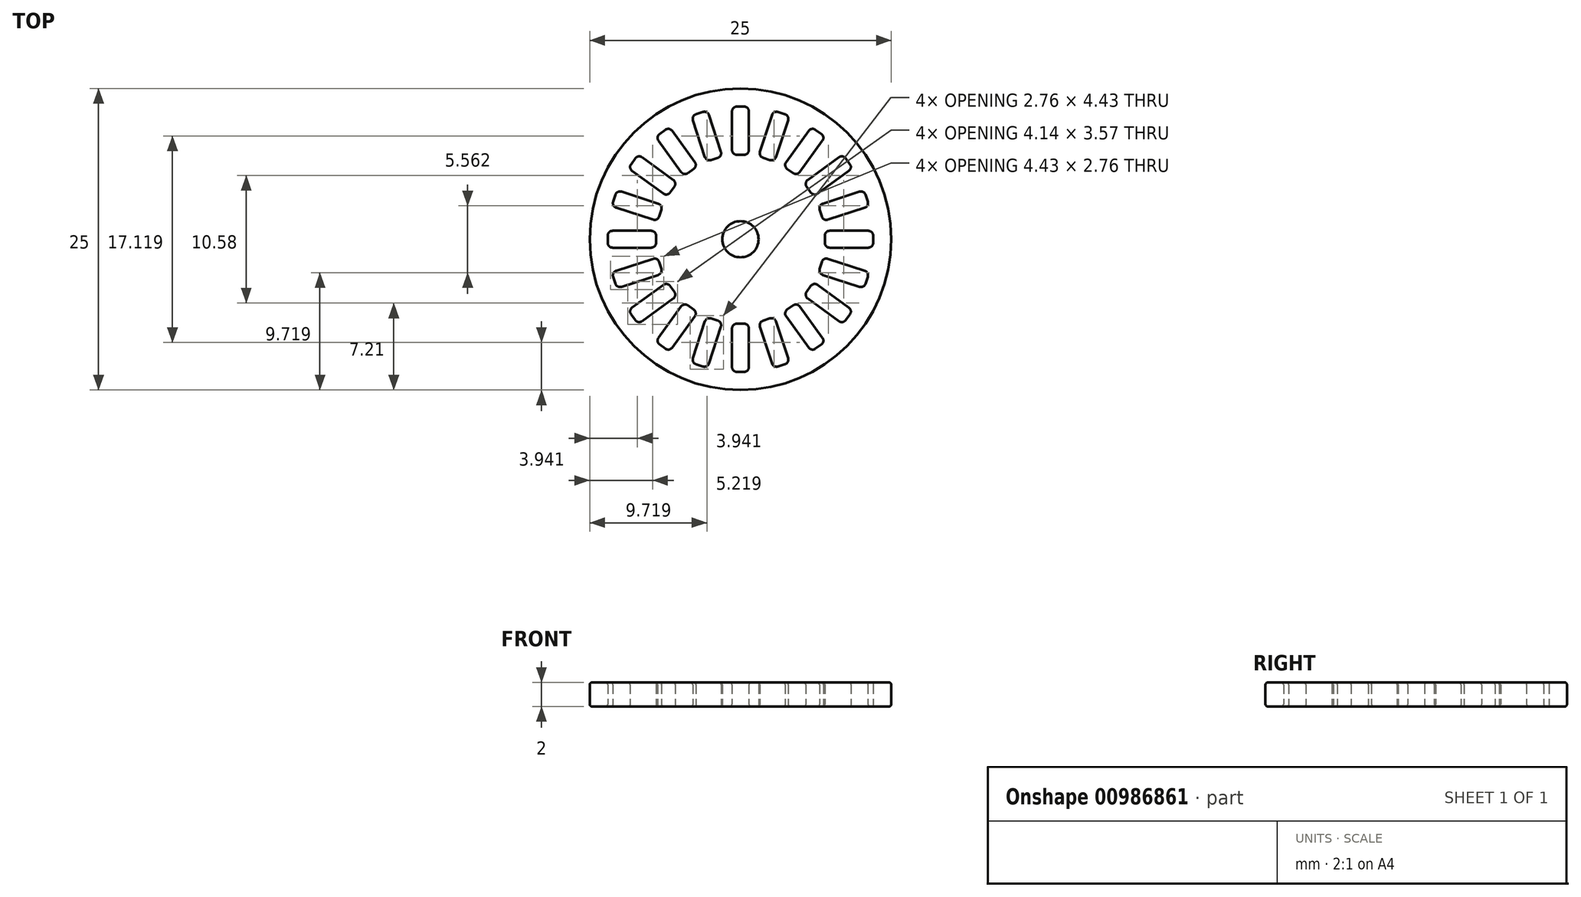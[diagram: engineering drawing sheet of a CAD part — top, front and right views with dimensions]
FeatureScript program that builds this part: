
annotation { "Feature Type Name" : "Feature", "Feature Type Description" : "" }
export const myFeature = defineFeature(function(context is Context, id is Id, definition is map)
    precondition{}
    {
        {
            var Q0;
            Q0=qCreatedBy(makeId("Top.planeOp"),FACE);
            var sketch = newSketch(context, id + "F0", { "sketchPlane" : qUnion([Q0])});
            skCircle(sketch, "E0", {"center": v(0, 0) * mm, "radius": 12.5 * mm});
            skCircle(sketch, "E1", {"center": v(0, 0) * mm, "radius": 9 * mm, "construction": true});
            skLineSegment(sketch, "E2.bottom", {"start": v(0.3, 11) * mm, "end": v(-0.3, 11) * mm});
            skLineSegment(sketch, "E2.top", {"start": v(0.3, 7) * mm, "end": v(-0.3, 7) * mm});
            skLineSegment(sketch, "E2.left", {"start": v(0.7, 10.6) * mm, "end": v(0.7, 7.4) * mm});
            skLineSegment(sketch, "E2.right", {"start": v(-0.7, 10.6) * mm, "end": v(-0.7, 7.4) * mm});
            skPoint(sketch, "E2.middle", {"position": v(0, 9) * mm});
            skPoint(sketch, "E3.visualSharp", {"position": v(-0.7, 11) * mm});
            skArc(sketch, "E3.filletArc", {"start": v(-0.3, 11) * mm, "mid": v(-0.58, 10.88) * mm, "end": v(-0.7, 10.6) * mm});
            skPoint(sketch, "E4.visualSharp", {"position": v(0.7, 11) * mm});
            skArc(sketch, "E4.filletArc", {"start": v(0.7, 10.6) * mm, "mid": v(0.58, 10.88) * mm, "end": v(0.3, 11) * mm});
            skPoint(sketch, "E5.visualSharp", {"position": v(0.7, 7) * mm});
            skArc(sketch, "E5.filletArc", {"start": v(0.3, 7) * mm, "mid": v(0.58, 7.12) * mm, "end": v(0.7, 7.4) * mm});
            skPoint(sketch, "E6.visualSharp", {"position": v(-0.7, 7) * mm});
            skArc(sketch, "E6.filletArc", {"start": v(-0.7, 7.4) * mm, "mid": v(-0.58, 7.12) * mm, "end": v(-0.3, 7) * mm});
            skLineSegment(sketch, "E7.1.0", {"start": v(-2.6, 10.3) * mm, "end": v(-1.62, 7.25) * mm});
            skPoint(sketch, "E7.1.1", {"position": v(-1.5, 6.87) * mm});
            skPoint(sketch, "E7.1.2", {"position": v(-2.78, 8.56) * mm});
            skPoint(sketch, "E7.1.3", {"position": v(-2.83, 6.44) * mm});
            skLineSegment(sketch, "E7.1.4", {"start": v(-3.94, 9.86) * mm, "end": v(-2.95, 6.82) * mm});
            skLineSegment(sketch, "E7.1.5", {"start": v(-1.88, 6.75) * mm, "end": v(-2.45, 6.56) * mm});
            skLineSegment(sketch, "E7.1.6", {"start": v(-3.11, 10.55) * mm, "end": v(-3.68, 10.37) * mm});
            skPoint(sketch, "E7.1.7", {"position": v(-4.06, 10.25) * mm});
            skPoint(sketch, "E7.1.8", {"position": v(-2.73, 10.68) * mm});
            skArc(sketch, "E7.1.9", {"start": v(-1.88, 6.75) * mm, "mid": v(-1.65, 6.95) * mm, "end": v(-1.62, 7.25) * mm});
            skArc(sketch, "E7.1.10", {"start": v(-3.68, 10.37) * mm, "mid": v(-3.92, 10.17) * mm, "end": v(-3.94, 9.86) * mm});
            skArc(sketch, "E7.1.11", {"start": v(-2.95, 6.82) * mm, "mid": v(-2.75, 6.59) * mm, "end": v(-2.45, 6.56) * mm});
            skArc(sketch, "E7.1.12", {"start": v(-2.6, 10.3) * mm, "mid": v(-2.8, 10.53) * mm, "end": v(-3.11, 10.55) * mm});
            skLineSegment(sketch, "E7.2.0", {"start": v(-5.66, 8.99) * mm, "end": v(-3.78, 6.4) * mm});
            skPoint(sketch, "E7.2.1", {"position": v(-3.55, 6.07) * mm});
            skPoint(sketch, "E7.2.2", {"position": v(-5.3, 7.28) * mm});
            skPoint(sketch, "E7.2.3", {"position": v(-4.68, 5.25) * mm});
            skLineSegment(sketch, "E7.2.4", {"start": v(-6.8, 8.16) * mm, "end": v(-4.92, 5.58) * mm});
            skLineSegment(sketch, "E7.2.5", {"start": v(-3.87, 5.84) * mm, "end": v(-4.36, 5.49) * mm});
            skLineSegment(sketch, "E7.2.6", {"start": v(-6.22, 9.08) * mm, "end": v(-6.7, 8.72) * mm});
            skPoint(sketch, "E7.2.7", {"position": v(-7.03, 8.49) * mm});
            skPoint(sketch, "E7.2.8", {"position": v(-5.9, 9.31) * mm});
            skArc(sketch, "E7.2.9", {"start": v(-3.87, 5.84) * mm, "mid": v(-3.71, 6.1) * mm, "end": v(-3.78, 6.4) * mm});
            skArc(sketch, "E7.2.10", {"start": v(-6.7, 8.72) * mm, "mid": v(-6.87, 8.46) * mm, "end": v(-6.8, 8.16) * mm});
            skArc(sketch, "E7.2.11", {"start": v(-4.92, 5.58) * mm, "mid": v(-4.65, 5.42) * mm, "end": v(-4.36, 5.49) * mm});
            skArc(sketch, "E7.2.12", {"start": v(-5.66, 8.99) * mm, "mid": v(-5.93, 9.15) * mm, "end": v(-6.22, 9.08) * mm});
            skLineSegment(sketch, "E7.3.0", {"start": v(-8.16, 6.8) * mm, "end": v(-5.58, 4.92) * mm});
            skPoint(sketch, "E7.3.1", {"position": v(-5.25, 4.68) * mm});
            skPoint(sketch, "E7.3.2", {"position": v(-7.28, 5.3) * mm});
            skPoint(sketch, "E7.3.3", {"position": v(-6.07, 3.55) * mm});
            skLineSegment(sketch, "E7.3.4", {"start": v(-8.99, 5.66) * mm, "end": v(-6.4, 3.78) * mm});
            skLineSegment(sketch, "E7.3.5", {"start": v(-5.49, 4.36) * mm, "end": v(-5.84, 3.87) * mm});
            skLineSegment(sketch, "E7.3.6", {"start": v(-8.72, 6.7) * mm, "end": v(-9.08, 6.22) * mm});
            skPoint(sketch, "E7.3.7", {"position": v(-9.31, 5.9) * mm});
            skPoint(sketch, "E7.3.8", {"position": v(-8.49, 7.03) * mm});
            skArc(sketch, "E7.3.9", {"start": v(-5.49, 4.36) * mm, "mid": v(-5.42, 4.65) * mm, "end": v(-5.58, 4.92) * mm});
            skArc(sketch, "E7.3.10", {"start": v(-9.08, 6.22) * mm, "mid": v(-9.15, 5.93) * mm, "end": v(-8.99, 5.66) * mm});
            skArc(sketch, "E7.3.11", {"start": v(-6.4, 3.78) * mm, "mid": v(-6.1, 3.71) * mm, "end": v(-5.84, 3.87) * mm});
            skArc(sketch, "E7.3.12", {"start": v(-8.16, 6.8) * mm, "mid": v(-8.46, 6.87) * mm, "end": v(-8.72, 6.7) * mm});
            skLineSegment(sketch, "E7.4.0", {"start": v(-9.86, 3.94) * mm, "end": v(-6.82, 2.95) * mm});
            skPoint(sketch, "E7.4.1", {"position": v(-6.44, 2.83) * mm});
            skPoint(sketch, "E7.4.2", {"position": v(-8.56, 2.78) * mm});
            skPoint(sketch, "E7.4.3", {"position": v(-6.87, 1.5) * mm});
            skLineSegment(sketch, "E7.4.4", {"start": v(-10.3, 2.6) * mm, "end": v(-7.25, 1.62) * mm});
            skLineSegment(sketch, "E7.4.5", {"start": v(-6.56, 2.45) * mm, "end": v(-6.75, 1.88) * mm});
            skLineSegment(sketch, "E7.4.6", {"start": v(-10.37, 3.68) * mm, "end": v(-10.55, 3.11) * mm});
            skPoint(sketch, "E7.4.7", {"position": v(-10.68, 2.73) * mm});
            skPoint(sketch, "E7.4.8", {"position": v(-10.25, 4.06) * mm});
            skArc(sketch, "E7.4.9", {"start": v(-6.56, 2.45) * mm, "mid": v(-6.59, 2.75) * mm, "end": v(-6.82, 2.95) * mm});
            skArc(sketch, "E7.4.10", {"start": v(-10.55, 3.11) * mm, "mid": v(-10.53, 2.8) * mm, "end": v(-10.3, 2.6) * mm});
            skArc(sketch, "E7.4.11", {"start": v(-7.25, 1.62) * mm, "mid": v(-6.95, 1.65) * mm, "end": v(-6.75, 1.88) * mm});
            skArc(sketch, "E7.4.12", {"start": v(-9.86, 3.94) * mm, "mid": v(-10.17, 3.92) * mm, "end": v(-10.37, 3.68) * mm});
            skLineSegment(sketch, "E7.5.0", {"start": v(-10.6, 0.7) * mm, "end": v(-7.4, 0.7) * mm});
            skPoint(sketch, "E7.5.1", {"position": v(-7, 0.7) * mm});
            skPoint(sketch, "E7.5.2", {"position": v(-9, 0) * mm});
            skPoint(sketch, "E7.5.3", {"position": v(-7, -0.7) * mm});
            skLineSegment(sketch, "E7.5.4", {"start": v(-10.6, -0.7) * mm, "end": v(-7.4, -0.7) * mm});
            skLineSegment(sketch, "E7.5.5", {"start": v(-7, 0.3) * mm, "end": v(-7, -0.3) * mm});
            skLineSegment(sketch, "E7.5.6", {"start": v(-11, 0.3) * mm, "end": v(-11, -0.3) * mm});
            skPoint(sketch, "E7.5.7", {"position": v(-11, -0.7) * mm});
            skPoint(sketch, "E7.5.8", {"position": v(-11, 0.7) * mm});
            skArc(sketch, "E7.5.9", {"start": v(-7, 0.3) * mm, "mid": v(-7.12, 0.58) * mm, "end": v(-7.4, 0.7) * mm});
            skArc(sketch, "E7.5.10", {"start": v(-11, -0.3) * mm, "mid": v(-10.88, -0.58) * mm, "end": v(-10.6, -0.7) * mm});
            skArc(sketch, "E7.5.11", {"start": v(-7.4, -0.7) * mm, "mid": v(-7.12, -0.58) * mm, "end": v(-7, -0.3) * mm});
            skArc(sketch, "E7.5.12", {"start": v(-10.6, 0.7) * mm, "mid": v(-10.88, 0.58) * mm, "end": v(-11, 0.3) * mm});
            skLineSegment(sketch, "E7.6.0", {"start": v(-10.3, -2.6) * mm, "end": v(-7.25, -1.62) * mm});
            skPoint(sketch, "E7.6.1", {"position": v(-6.87, -1.5) * mm});
            skPoint(sketch, "E7.6.2", {"position": v(-8.56, -2.78) * mm});
            skPoint(sketch, "E7.6.3", {"position": v(-6.44, -2.83) * mm});
            skLineSegment(sketch, "E7.6.4", {"start": v(-9.86, -3.94) * mm, "end": v(-6.82, -2.95) * mm});
            skLineSegment(sketch, "E7.6.5", {"start": v(-6.75, -1.88) * mm, "end": v(-6.56, -2.45) * mm});
            skLineSegment(sketch, "E7.6.6", {"start": v(-10.55, -3.11) * mm, "end": v(-10.37, -3.68) * mm});
            skPoint(sketch, "E7.6.7", {"position": v(-10.25, -4.06) * mm});
            skPoint(sketch, "E7.6.8", {"position": v(-10.68, -2.73) * mm});
            skArc(sketch, "E7.6.9", {"start": v(-6.75, -1.88) * mm, "mid": v(-6.95, -1.65) * mm, "end": v(-7.25, -1.62) * mm});
            skArc(sketch, "E7.6.10", {"start": v(-10.37, -3.68) * mm, "mid": v(-10.17, -3.92) * mm, "end": v(-9.86, -3.94) * mm});
            skArc(sketch, "E7.6.11", {"start": v(-6.82, -2.95) * mm, "mid": v(-6.59, -2.75) * mm, "end": v(-6.56, -2.45) * mm});
            skArc(sketch, "E7.6.12", {"start": v(-10.3, -2.6) * mm, "mid": v(-10.53, -2.8) * mm, "end": v(-10.55, -3.11) * mm});
            skLineSegment(sketch, "E7.7.0", {"start": v(-8.99, -5.66) * mm, "end": v(-6.4, -3.78) * mm});
            skPoint(sketch, "E7.7.1", {"position": v(-6.07, -3.55) * mm});
            skPoint(sketch, "E7.7.2", {"position": v(-7.28, -5.3) * mm});
            skPoint(sketch, "E7.7.3", {"position": v(-5.25, -4.68) * mm});
            skLineSegment(sketch, "E7.7.4", {"start": v(-8.16, -6.8) * mm, "end": v(-5.58, -4.92) * mm});
            skLineSegment(sketch, "E7.7.5", {"start": v(-5.84, -3.87) * mm, "end": v(-5.49, -4.36) * mm});
            skLineSegment(sketch, "E7.7.6", {"start": v(-9.08, -6.22) * mm, "end": v(-8.72, -6.7) * mm});
            skPoint(sketch, "E7.7.7", {"position": v(-8.49, -7.03) * mm});
            skPoint(sketch, "E7.7.8", {"position": v(-9.31, -5.9) * mm});
            skArc(sketch, "E7.7.9", {"start": v(-5.84, -3.87) * mm, "mid": v(-6.1, -3.71) * mm, "end": v(-6.4, -3.78) * mm});
            skArc(sketch, "E7.7.10", {"start": v(-8.72, -6.7) * mm, "mid": v(-8.46, -6.87) * mm, "end": v(-8.16, -6.8) * mm});
            skArc(sketch, "E7.7.11", {"start": v(-5.58, -4.92) * mm, "mid": v(-5.42, -4.65) * mm, "end": v(-5.49, -4.36) * mm});
            skArc(sketch, "E7.7.12", {"start": v(-8.99, -5.66) * mm, "mid": v(-9.15, -5.93) * mm, "end": v(-9.08, -6.22) * mm});
            skLineSegment(sketch, "E7.8.0", {"start": v(-6.8, -8.16) * mm, "end": v(-4.92, -5.58) * mm});
            skPoint(sketch, "E7.8.1", {"position": v(-4.68, -5.25) * mm});
            skPoint(sketch, "E7.8.2", {"position": v(-5.3, -7.28) * mm});
            skPoint(sketch, "E7.8.3", {"position": v(-3.55, -6.07) * mm});
            skLineSegment(sketch, "E7.8.4", {"start": v(-5.66, -8.99) * mm, "end": v(-3.78, -6.4) * mm});
            skLineSegment(sketch, "E7.8.5", {"start": v(-4.36, -5.49) * mm, "end": v(-3.87, -5.84) * mm});
            skLineSegment(sketch, "E7.8.6", {"start": v(-6.7, -8.72) * mm, "end": v(-6.22, -9.08) * mm});
            skPoint(sketch, "E7.8.7", {"position": v(-5.9, -9.31) * mm});
            skPoint(sketch, "E7.8.8", {"position": v(-7.03, -8.49) * mm});
            skArc(sketch, "E7.8.9", {"start": v(-4.36, -5.49) * mm, "mid": v(-4.65, -5.42) * mm, "end": v(-4.92, -5.58) * mm});
            skArc(sketch, "E7.8.10", {"start": v(-6.22, -9.08) * mm, "mid": v(-5.93, -9.15) * mm, "end": v(-5.66, -8.99) * mm});
            skArc(sketch, "E7.8.11", {"start": v(-3.78, -6.4) * mm, "mid": v(-3.71, -6.1) * mm, "end": v(-3.87, -5.84) * mm});
            skArc(sketch, "E7.8.12", {"start": v(-6.8, -8.16) * mm, "mid": v(-6.87, -8.46) * mm, "end": v(-6.7, -8.72) * mm});
            skLineSegment(sketch, "E7.9.0", {"start": v(-3.94, -9.86) * mm, "end": v(-2.95, -6.82) * mm});
            skPoint(sketch, "E7.9.1", {"position": v(-2.83, -6.44) * mm});
            skPoint(sketch, "E7.9.2", {"position": v(-2.78, -8.56) * mm});
            skPoint(sketch, "E7.9.3", {"position": v(-1.5, -6.87) * mm});
            skLineSegment(sketch, "E7.9.4", {"start": v(-2.6, -10.3) * mm, "end": v(-1.62, -7.25) * mm});
            skLineSegment(sketch, "E7.9.5", {"start": v(-2.45, -6.56) * mm, "end": v(-1.88, -6.75) * mm});
            skLineSegment(sketch, "E7.9.6", {"start": v(-3.68, -10.37) * mm, "end": v(-3.11, -10.55) * mm});
            skPoint(sketch, "E7.9.7", {"position": v(-2.73, -10.68) * mm});
            skPoint(sketch, "E7.9.8", {"position": v(-4.06, -10.25) * mm});
            skArc(sketch, "E7.9.9", {"start": v(-2.45, -6.56) * mm, "mid": v(-2.75, -6.59) * mm, "end": v(-2.95, -6.82) * mm});
            skArc(sketch, "E7.9.10", {"start": v(-3.11, -10.55) * mm, "mid": v(-2.8, -10.53) * mm, "end": v(-2.6, -10.3) * mm});
            skArc(sketch, "E7.9.11", {"start": v(-1.62, -7.25) * mm, "mid": v(-1.65, -6.95) * mm, "end": v(-1.88, -6.75) * mm});
            skArc(sketch, "E7.9.12", {"start": v(-3.94, -9.86) * mm, "mid": v(-3.92, -10.17) * mm, "end": v(-3.68, -10.37) * mm});
            skLineSegment(sketch, "E7.10.0", {"start": v(-0.7, -10.6) * mm, "end": v(-0.7, -7.4) * mm});
            skPoint(sketch, "E7.10.1", {"position": v(-0.7, -7) * mm});
            skPoint(sketch, "E7.10.2", {"position": v(0, -9) * mm});
            skPoint(sketch, "E7.10.3", {"position": v(0.7, -7) * mm});
            skLineSegment(sketch, "E7.10.4", {"start": v(0.7, -10.6) * mm, "end": v(0.7, -7.4) * mm});
            skLineSegment(sketch, "E7.10.5", {"start": v(-0.3, -7) * mm, "end": v(0.3, -7) * mm});
            skLineSegment(sketch, "E7.10.6", {"start": v(-0.3, -11) * mm, "end": v(0.3, -11) * mm});
            skPoint(sketch, "E7.10.7", {"position": v(0.7, -11) * mm});
            skPoint(sketch, "E7.10.8", {"position": v(-0.7, -11) * mm});
            skArc(sketch, "E7.10.9", {"start": v(-0.3, -7) * mm, "mid": v(-0.58, -7.12) * mm, "end": v(-0.7, -7.4) * mm});
            skArc(sketch, "E7.10.10", {"start": v(0.3, -11) * mm, "mid": v(0.58, -10.88) * mm, "end": v(0.7, -10.6) * mm});
            skArc(sketch, "E7.10.11", {"start": v(0.7, -7.4) * mm, "mid": v(0.58, -7.12) * mm, "end": v(0.3, -7) * mm});
            skArc(sketch, "E7.10.12", {"start": v(-0.7, -10.6) * mm, "mid": v(-0.58, -10.88) * mm, "end": v(-0.3, -11) * mm});
            skLineSegment(sketch, "E7.11.0", {"start": v(2.6, -10.3) * mm, "end": v(1.62, -7.25) * mm});
            skPoint(sketch, "E7.11.1", {"position": v(1.5, -6.87) * mm});
            skPoint(sketch, "E7.11.2", {"position": v(2.78, -8.56) * mm});
            skPoint(sketch, "E7.11.3", {"position": v(2.83, -6.44) * mm});
            skLineSegment(sketch, "E7.11.4", {"start": v(3.94, -9.86) * mm, "end": v(2.95, -6.82) * mm});
            skLineSegment(sketch, "E7.11.5", {"start": v(1.88, -6.75) * mm, "end": v(2.45, -6.56) * mm});
            skLineSegment(sketch, "E7.11.6", {"start": v(3.11, -10.55) * mm, "end": v(3.68, -10.37) * mm});
            skPoint(sketch, "E7.11.7", {"position": v(4.06, -10.25) * mm});
            skPoint(sketch, "E7.11.8", {"position": v(2.73, -10.68) * mm});
            skArc(sketch, "E7.11.9", {"start": v(1.88, -6.75) * mm, "mid": v(1.65, -6.95) * mm, "end": v(1.62, -7.25) * mm});
            skArc(sketch, "E7.11.10", {"start": v(3.68, -10.37) * mm, "mid": v(3.92, -10.17) * mm, "end": v(3.94, -9.86) * mm});
            skArc(sketch, "E7.11.11", {"start": v(2.95, -6.82) * mm, "mid": v(2.75, -6.59) * mm, "end": v(2.45, -6.56) * mm});
            skArc(sketch, "E7.11.12", {"start": v(2.6, -10.3) * mm, "mid": v(2.8, -10.53) * mm, "end": v(3.11, -10.55) * mm});
            skLineSegment(sketch, "E7.12.0", {"start": v(5.66, -8.99) * mm, "end": v(3.78, -6.4) * mm});
            skPoint(sketch, "E7.12.1", {"position": v(3.55, -6.07) * mm});
            skPoint(sketch, "E7.12.2", {"position": v(5.3, -7.28) * mm});
            skPoint(sketch, "E7.12.3", {"position": v(4.68, -5.25) * mm});
            skLineSegment(sketch, "E7.12.4", {"start": v(6.8, -8.16) * mm, "end": v(4.92, -5.58) * mm});
            skLineSegment(sketch, "E7.12.5", {"start": v(3.87, -5.84) * mm, "end": v(4.36, -5.49) * mm});
            skLineSegment(sketch, "E7.12.6", {"start": v(6.22, -9.08) * mm, "end": v(6.7, -8.72) * mm});
            skPoint(sketch, "E7.12.7", {"position": v(7.03, -8.49) * mm});
            skPoint(sketch, "E7.12.8", {"position": v(5.9, -9.31) * mm});
            skArc(sketch, "E7.12.9", {"start": v(3.87, -5.84) * mm, "mid": v(3.71, -6.1) * mm, "end": v(3.78, -6.4) * mm});
            skArc(sketch, "E7.12.10", {"start": v(6.7, -8.72) * mm, "mid": v(6.87, -8.46) * mm, "end": v(6.8, -8.16) * mm});
            skArc(sketch, "E7.12.11", {"start": v(4.92, -5.58) * mm, "mid": v(4.65, -5.42) * mm, "end": v(4.36, -5.49) * mm});
            skArc(sketch, "E7.12.12", {"start": v(5.66, -8.99) * mm, "mid": v(5.93, -9.15) * mm, "end": v(6.22, -9.08) * mm});
            skLineSegment(sketch, "E7.13.0", {"start": v(8.16, -6.8) * mm, "end": v(5.58, -4.92) * mm});
            skPoint(sketch, "E7.13.1", {"position": v(5.25, -4.68) * mm});
            skPoint(sketch, "E7.13.2", {"position": v(7.28, -5.3) * mm});
            skPoint(sketch, "E7.13.3", {"position": v(6.07, -3.55) * mm});
            skLineSegment(sketch, "E7.13.4", {"start": v(8.99, -5.66) * mm, "end": v(6.4, -3.78) * mm});
            skLineSegment(sketch, "E7.13.5", {"start": v(5.49, -4.36) * mm, "end": v(5.84, -3.87) * mm});
            skLineSegment(sketch, "E7.13.6", {"start": v(8.72, -6.7) * mm, "end": v(9.08, -6.22) * mm});
            skPoint(sketch, "E7.13.7", {"position": v(9.31, -5.9) * mm});
            skPoint(sketch, "E7.13.8", {"position": v(8.49, -7.03) * mm});
            skArc(sketch, "E7.13.9", {"start": v(5.49, -4.36) * mm, "mid": v(5.42, -4.65) * mm, "end": v(5.58, -4.92) * mm});
            skArc(sketch, "E7.13.10", {"start": v(9.08, -6.22) * mm, "mid": v(9.15, -5.93) * mm, "end": v(8.99, -5.66) * mm});
            skArc(sketch, "E7.13.11", {"start": v(6.4, -3.78) * mm, "mid": v(6.1, -3.71) * mm, "end": v(5.84, -3.87) * mm});
            skArc(sketch, "E7.13.12", {"start": v(8.16, -6.8) * mm, "mid": v(8.46, -6.87) * mm, "end": v(8.72, -6.7) * mm});
            skLineSegment(sketch, "E7.14.0", {"start": v(9.86, -3.94) * mm, "end": v(6.82, -2.95) * mm});
            skPoint(sketch, "E7.14.1", {"position": v(6.44, -2.83) * mm});
            skPoint(sketch, "E7.14.2", {"position": v(8.56, -2.78) * mm});
            skPoint(sketch, "E7.14.3", {"position": v(6.87, -1.5) * mm});
            skLineSegment(sketch, "E7.14.4", {"start": v(10.3, -2.6) * mm, "end": v(7.25, -1.62) * mm});
            skLineSegment(sketch, "E7.14.5", {"start": v(6.56, -2.45) * mm, "end": v(6.75, -1.88) * mm});
            skLineSegment(sketch, "E7.14.6", {"start": v(10.37, -3.68) * mm, "end": v(10.55, -3.11) * mm});
            skPoint(sketch, "E7.14.7", {"position": v(10.68, -2.73) * mm});
            skPoint(sketch, "E7.14.8", {"position": v(10.25, -4.06) * mm});
            skArc(sketch, "E7.14.9", {"start": v(6.56, -2.45) * mm, "mid": v(6.59, -2.75) * mm, "end": v(6.82, -2.95) * mm});
            skArc(sketch, "E7.14.10", {"start": v(10.55, -3.11) * mm, "mid": v(10.53, -2.8) * mm, "end": v(10.3, -2.6) * mm});
            skArc(sketch, "E7.14.11", {"start": v(7.25, -1.62) * mm, "mid": v(6.95, -1.65) * mm, "end": v(6.75, -1.88) * mm});
            skArc(sketch, "E7.14.12", {"start": v(9.86, -3.94) * mm, "mid": v(10.17, -3.92) * mm, "end": v(10.37, -3.68) * mm});
            skLineSegment(sketch, "E7.15.0", {"start": v(10.6, -0.7) * mm, "end": v(7.4, -0.7) * mm});
            skPoint(sketch, "E7.15.1", {"position": v(7, -0.7) * mm});
            skPoint(sketch, "E7.15.2", {"position": v(9, 0) * mm});
            skPoint(sketch, "E7.15.3", {"position": v(7, 0.7) * mm});
            skLineSegment(sketch, "E7.15.4", {"start": v(10.6, 0.7) * mm, "end": v(7.4, 0.7) * mm});
            skLineSegment(sketch, "E7.15.5", {"start": v(7, -0.3) * mm, "end": v(7, 0.3) * mm});
            skLineSegment(sketch, "E7.15.6", {"start": v(11, -0.3) * mm, "end": v(11, 0.3) * mm});
            skPoint(sketch, "E7.15.7", {"position": v(11, 0.7) * mm});
            skPoint(sketch, "E7.15.8", {"position": v(11, -0.7) * mm});
            skArc(sketch, "E7.15.9", {"start": v(7, -0.3) * mm, "mid": v(7.12, -0.58) * mm, "end": v(7.4, -0.7) * mm});
            skArc(sketch, "E7.15.10", {"start": v(11, 0.3) * mm, "mid": v(10.88, 0.58) * mm, "end": v(10.6, 0.7) * mm});
            skArc(sketch, "E7.15.11", {"start": v(7.4, 0.7) * mm, "mid": v(7.12, 0.58) * mm, "end": v(7, 0.3) * mm});
            skArc(sketch, "E7.15.12", {"start": v(10.6, -0.7) * mm, "mid": v(10.88, -0.58) * mm, "end": v(11, -0.3) * mm});
            skLineSegment(sketch, "E7.16.0", {"start": v(10.3, 2.6) * mm, "end": v(7.25, 1.62) * mm});
            skPoint(sketch, "E7.16.1", {"position": v(6.87, 1.5) * mm});
            skPoint(sketch, "E7.16.2", {"position": v(8.56, 2.78) * mm});
            skPoint(sketch, "E7.16.3", {"position": v(6.44, 2.83) * mm});
            skLineSegment(sketch, "E7.16.4", {"start": v(9.86, 3.94) * mm, "end": v(6.82, 2.95) * mm});
            skLineSegment(sketch, "E7.16.5", {"start": v(6.75, 1.88) * mm, "end": v(6.56, 2.45) * mm});
            skLineSegment(sketch, "E7.16.6", {"start": v(10.55, 3.11) * mm, "end": v(10.37, 3.68) * mm});
            skPoint(sketch, "E7.16.7", {"position": v(10.25, 4.06) * mm});
            skPoint(sketch, "E7.16.8", {"position": v(10.68, 2.73) * mm});
            skArc(sketch, "E7.16.9", {"start": v(6.75, 1.88) * mm, "mid": v(6.95, 1.65) * mm, "end": v(7.25, 1.62) * mm});
            skArc(sketch, "E7.16.10", {"start": v(10.37, 3.68) * mm, "mid": v(10.17, 3.92) * mm, "end": v(9.86, 3.94) * mm});
            skArc(sketch, "E7.16.11", {"start": v(6.82, 2.95) * mm, "mid": v(6.59, 2.75) * mm, "end": v(6.56, 2.45) * mm});
            skArc(sketch, "E7.16.12", {"start": v(10.3, 2.6) * mm, "mid": v(10.53, 2.8) * mm, "end": v(10.55, 3.11) * mm});
            skLineSegment(sketch, "E7.17.0", {"start": v(8.99, 5.66) * mm, "end": v(6.4, 3.78) * mm});
            skPoint(sketch, "E7.17.1", {"position": v(6.07, 3.55) * mm});
            skPoint(sketch, "E7.17.2", {"position": v(7.28, 5.3) * mm});
            skPoint(sketch, "E7.17.3", {"position": v(5.25, 4.68) * mm});
            skLineSegment(sketch, "E7.17.4", {"start": v(8.16, 6.8) * mm, "end": v(5.58, 4.92) * mm});
            skLineSegment(sketch, "E7.17.5", {"start": v(5.84, 3.87) * mm, "end": v(5.49, 4.36) * mm});
            skLineSegment(sketch, "E7.17.6", {"start": v(9.08, 6.22) * mm, "end": v(8.72, 6.7) * mm});
            skPoint(sketch, "E7.17.7", {"position": v(8.49, 7.03) * mm});
            skPoint(sketch, "E7.17.8", {"position": v(9.31, 5.9) * mm});
            skArc(sketch, "E7.17.9", {"start": v(5.84, 3.87) * mm, "mid": v(6.1, 3.71) * mm, "end": v(6.4, 3.78) * mm});
            skArc(sketch, "E7.17.10", {"start": v(8.72, 6.7) * mm, "mid": v(8.46, 6.87) * mm, "end": v(8.16, 6.8) * mm});
            skArc(sketch, "E7.17.11", {"start": v(5.58, 4.92) * mm, "mid": v(5.42, 4.65) * mm, "end": v(5.49, 4.36) * mm});
            skArc(sketch, "E7.17.12", {"start": v(8.99, 5.66) * mm, "mid": v(9.15, 5.93) * mm, "end": v(9.08, 6.22) * mm});
            skLineSegment(sketch, "E7.18.0", {"start": v(6.8, 8.16) * mm, "end": v(4.92, 5.58) * mm});
            skPoint(sketch, "E7.18.1", {"position": v(4.68, 5.25) * mm});
            skPoint(sketch, "E7.18.2", {"position": v(5.3, 7.28) * mm});
            skPoint(sketch, "E7.18.3", {"position": v(3.55, 6.07) * mm});
            skLineSegment(sketch, "E7.18.4", {"start": v(5.66, 8.99) * mm, "end": v(3.78, 6.4) * mm});
            skLineSegment(sketch, "E7.18.5", {"start": v(4.36, 5.49) * mm, "end": v(3.87, 5.84) * mm});
            skLineSegment(sketch, "E7.18.6", {"start": v(6.7, 8.72) * mm, "end": v(6.22, 9.08) * mm});
            skPoint(sketch, "E7.18.7", {"position": v(5.9, 9.31) * mm});
            skPoint(sketch, "E7.18.8", {"position": v(7.03, 8.49) * mm});
            skArc(sketch, "E7.18.9", {"start": v(4.36, 5.49) * mm, "mid": v(4.65, 5.42) * mm, "end": v(4.92, 5.58) * mm});
            skArc(sketch, "E7.18.10", {"start": v(6.22, 9.08) * mm, "mid": v(5.93, 9.15) * mm, "end": v(5.66, 8.99) * mm});
            skArc(sketch, "E7.18.11", {"start": v(3.78, 6.4) * mm, "mid": v(3.71, 6.1) * mm, "end": v(3.87, 5.84) * mm});
            skArc(sketch, "E7.18.12", {"start": v(6.8, 8.16) * mm, "mid": v(6.87, 8.46) * mm, "end": v(6.7, 8.72) * mm});
            skLineSegment(sketch, "E7.19.0", {"start": v(3.94, 9.86) * mm, "end": v(2.95, 6.82) * mm});
            skPoint(sketch, "E7.19.1", {"position": v(2.83, 6.44) * mm});
            skPoint(sketch, "E7.19.2", {"position": v(2.78, 8.56) * mm});
            skPoint(sketch, "E7.19.3", {"position": v(1.5, 6.87) * mm});
            skLineSegment(sketch, "E7.19.4", {"start": v(2.6, 10.3) * mm, "end": v(1.62, 7.25) * mm});
            skLineSegment(sketch, "E7.19.5", {"start": v(2.45, 6.56) * mm, "end": v(1.88, 6.75) * mm});
            skLineSegment(sketch, "E7.19.6", {"start": v(3.68, 10.37) * mm, "end": v(3.11, 10.55) * mm});
            skPoint(sketch, "E7.19.7", {"position": v(2.73, 10.68) * mm});
            skPoint(sketch, "E7.19.8", {"position": v(4.06, 10.25) * mm});
            skArc(sketch, "E7.19.9", {"start": v(2.45, 6.56) * mm, "mid": v(2.75, 6.59) * mm, "end": v(2.95, 6.82) * mm});
            skArc(sketch, "E7.19.10", {"start": v(3.11, 10.55) * mm, "mid": v(2.8, 10.53) * mm, "end": v(2.6, 10.3) * mm});
            skArc(sketch, "E7.19.11", {"start": v(1.62, 7.25) * mm, "mid": v(1.65, 6.95) * mm, "end": v(1.88, 6.75) * mm});
            skArc(sketch, "E7.19.12", {"start": v(3.94, 9.86) * mm, "mid": v(3.92, 10.17) * mm, "end": v(3.68, 10.37) * mm});
            skCircle(sketch, "E8", {"center": v(0, 0) * mm, "radius": 1.5 * mm});
            skSolve(sketch);
        }
        {
            var Q0;
            Q0=makeQuery(id+"F0.imprint","IMPRINT",FACE,{"disambiguationData":[TD([[makeQuery(id+"F0.imprint","IMPRINT",EDGE,{"derivedFrom":sQuery(id+"F0.wireOp",EDGE,"E0")}),1.0]])]});
            extrude(context, id + "F1", {"entities" : qUnion([Q0]), "depth" : 2 * mm, "offsetDistance" : 25 * mm});
        }
        {
            var Q0;
            Q0=makeQuery(id+"F1.opExtrude","CAP_FACE",FACE,{"disambiguationData":[OSD([sQuery(id+"F0.wireOp",EDGE,"E0"),sQuery(id+"F0.wireOp",EDGE,"E2.bottom"),sQuery(id+"F0.wireOp",EDGE,"E2.top"),sQuery(id+"F0.wireOp",EDGE,"E2.left"),sQuery(id+"F0.wireOp",EDGE,"E2.right"),sQuery(id+"F0.wireOp",EDGE,"E3.filletArc"),sQuery(id+"F0.wireOp",EDGE,"E4.filletArc"),sQuery(id+"F0.wireOp",EDGE,"E5.filletArc"),sQuery(id+"F0.wireOp",EDGE,"E6.filletArc"),sQuery(id+"F0.wireOp",EDGE,"E7.1.0"),sQuery(id+"F0.wireOp",EDGE,"E7.1.4"),sQuery(id+"F0.wireOp",EDGE,"E7.1.5"),sQuery(id+"F0.wireOp",EDGE,"E7.1.6"),sQuery(id+"F0.wireOp",EDGE,"E7.1.9"),sQuery(id+"F0.wireOp",EDGE,"E7.1.10"),sQuery(id+"F0.wireOp",EDGE,"E7.1.11"),sQuery(id+"F0.wireOp",EDGE,"E7.1.12"),sQuery(id+"F0.wireOp",EDGE,"E7.2.0"),sQuery(id+"F0.wireOp",EDGE,"E7.2.4"),sQuery(id+"F0.wireOp",EDGE,"E7.2.5"),sQuery(id+"F0.wireOp",EDGE,"E7.2.6"),sQuery(id+"F0.wireOp",EDGE,"E7.2.9"),sQuery(id+"F0.wireOp",EDGE,"E7.2.10"),sQuery(id+"F0.wireOp",EDGE,"E7.2.11"),sQuery(id+"F0.wireOp",EDGE,"E7.2.12"),sQuery(id+"F0.wireOp",EDGE,"E7.3.0"),sQuery(id+"F0.wireOp",EDGE,"E7.3.4"),sQuery(id+"F0.wireOp",EDGE,"E7.3.5"),sQuery(id+"F0.wireOp",EDGE,"E7.3.6"),sQuery(id+"F0.wireOp",EDGE,"E7.3.9"),sQuery(id+"F0.wireOp",EDGE,"E7.3.10"),sQuery(id+"F0.wireOp",EDGE,"E7.3.11"),sQuery(id+"F0.wireOp",EDGE,"E7.3.12"),sQuery(id+"F0.wireOp",EDGE,"E7.4.0"),sQuery(id+"F0.wireOp",EDGE,"E7.4.4"),sQuery(id+"F0.wireOp",EDGE,"E7.4.5"),sQuery(id+"F0.wireOp",EDGE,"E7.4.6"),sQuery(id+"F0.wireOp",EDGE,"E7.4.9"),sQuery(id+"F0.wireOp",EDGE,"E7.4.10"),sQuery(id+"F0.wireOp",EDGE,"E7.4.11"),sQuery(id+"F0.wireOp",EDGE,"E7.4.12"),sQuery(id+"F0.wireOp",EDGE,"E7.5.0"),sQuery(id+"F0.wireOp",EDGE,"E7.5.4"),sQuery(id+"F0.wireOp",EDGE,"E7.5.5"),sQuery(id+"F0.wireOp",EDGE,"E7.5.6"),sQuery(id+"F0.wireOp",EDGE,"E7.5.9"),sQuery(id+"F0.wireOp",EDGE,"E7.5.10"),sQuery(id+"F0.wireOp",EDGE,"E7.5.11"),sQuery(id+"F0.wireOp",EDGE,"E7.5.12"),sQuery(id+"F0.wireOp",EDGE,"E7.6.0"),sQuery(id+"F0.wireOp",EDGE,"E7.6.4"),sQuery(id+"F0.wireOp",EDGE,"E7.6.5"),sQuery(id+"F0.wireOp",EDGE,"E7.6.6"),sQuery(id+"F0.wireOp",EDGE,"E7.6.9"),sQuery(id+"F0.wireOp",EDGE,"E7.6.10"),sQuery(id+"F0.wireOp",EDGE,"E7.6.11"),sQuery(id+"F0.wireOp",EDGE,"E7.6.12"),sQuery(id+"F0.wireOp",EDGE,"E7.7.0"),sQuery(id+"F0.wireOp",EDGE,"E7.7.4"),sQuery(id+"F0.wireOp",EDGE,"E7.7.5"),sQuery(id+"F0.wireOp",EDGE,"E7.7.6"),sQuery(id+"F0.wireOp",EDGE,"E7.7.9"),sQuery(id+"F0.wireOp",EDGE,"E7.7.10"),sQuery(id+"F0.wireOp",EDGE,"E7.7.11"),sQuery(id+"F0.wireOp",EDGE,"E7.7.12"),sQuery(id+"F0.wireOp",EDGE,"E7.8.0"),sQuery(id+"F0.wireOp",EDGE,"E7.8.4"),sQuery(id+"F0.wireOp",EDGE,"E7.8.5"),sQuery(id+"F0.wireOp",EDGE,"E7.8.6"),sQuery(id+"F0.wireOp",EDGE,"E7.8.9"),sQuery(id+"F0.wireOp",EDGE,"E7.8.10"),sQuery(id+"F0.wireOp",EDGE,"E7.8.11"),sQuery(id+"F0.wireOp",EDGE,"E7.8.12"),sQuery(id+"F0.wireOp",EDGE,"E7.9.0"),sQuery(id+"F0.wireOp",EDGE,"E7.9.4"),sQuery(id+"F0.wireOp",EDGE,"E7.9.5"),sQuery(id+"F0.wireOp",EDGE,"E7.9.6"),sQuery(id+"F0.wireOp",EDGE,"E7.9.9"),sQuery(id+"F0.wireOp",EDGE,"E7.9.10"),sQuery(id+"F0.wireOp",EDGE,"E7.9.11"),sQuery(id+"F0.wireOp",EDGE,"E7.9.12"),sQuery(id+"F0.wireOp",EDGE,"E7.10.0"),sQuery(id+"F0.wireOp",EDGE,"E7.10.4"),sQuery(id+"F0.wireOp",EDGE,"E7.10.5"),sQuery(id+"F0.wireOp",EDGE,"E7.10.6"),sQuery(id+"F0.wireOp",EDGE,"E7.10.9"),sQuery(id+"F0.wireOp",EDGE,"E7.10.10"),sQuery(id+"F0.wireOp",EDGE,"E7.10.11"),sQuery(id+"F0.wireOp",EDGE,"E7.10.12"),sQuery(id+"F0.wireOp",EDGE,"E7.11.0"),sQuery(id+"F0.wireOp",EDGE,"E7.11.4"),sQuery(id+"F0.wireOp",EDGE,"E7.11.5"),sQuery(id+"F0.wireOp",EDGE,"E7.11.6"),sQuery(id+"F0.wireOp",EDGE,"E7.11.9"),sQuery(id+"F0.wireOp",EDGE,"E7.11.10"),sQuery(id+"F0.wireOp",EDGE,"E7.11.11"),sQuery(id+"F0.wireOp",EDGE,"E7.11.12"),sQuery(id+"F0.wireOp",EDGE,"E7.12.0"),sQuery(id+"F0.wireOp",EDGE,"E7.12.4"),sQuery(id+"F0.wireOp",EDGE,"E7.12.5"),sQuery(id+"F0.wireOp",EDGE,"E7.12.6"),sQuery(id+"F0.wireOp",EDGE,"E7.12.9"),sQuery(id+"F0.wireOp",EDGE,"E7.12.10"),sQuery(id+"F0.wireOp",EDGE,"E7.12.11"),sQuery(id+"F0.wireOp",EDGE,"E7.12.12"),sQuery(id+"F0.wireOp",EDGE,"E7.13.0"),sQuery(id+"F0.wireOp",EDGE,"E7.13.4"),sQuery(id+"F0.wireOp",EDGE,"E7.13.5"),sQuery(id+"F0.wireOp",EDGE,"E7.13.6"),sQuery(id+"F0.wireOp",EDGE,"E7.13.9"),sQuery(id+"F0.wireOp",EDGE,"E7.13.10"),sQuery(id+"F0.wireOp",EDGE,"E7.13.11"),sQuery(id+"F0.wireOp",EDGE,"E7.13.12"),sQuery(id+"F0.wireOp",EDGE,"E7.14.0"),sQuery(id+"F0.wireOp",EDGE,"E7.14.4"),sQuery(id+"F0.wireOp",EDGE,"E7.14.5"),sQuery(id+"F0.wireOp",EDGE,"E7.14.6"),sQuery(id+"F0.wireOp",EDGE,"E7.14.9"),sQuery(id+"F0.wireOp",EDGE,"E7.14.10"),sQuery(id+"F0.wireOp",EDGE,"E7.14.11"),sQuery(id+"F0.wireOp",EDGE,"E7.14.12"),sQuery(id+"F0.wireOp",EDGE,"E7.15.0"),sQuery(id+"F0.wireOp",EDGE,"E7.15.4"),sQuery(id+"F0.wireOp",EDGE,"E7.15.5"),sQuery(id+"F0.wireOp",EDGE,"E7.15.6"),sQuery(id+"F0.wireOp",EDGE,"E7.15.9"),sQuery(id+"F0.wireOp",EDGE,"E7.15.10"),sQuery(id+"F0.wireOp",EDGE,"E7.15.11"),sQuery(id+"F0.wireOp",EDGE,"E7.15.12"),sQuery(id+"F0.wireOp",EDGE,"E7.16.0"),sQuery(id+"F0.wireOp",EDGE,"E7.16.4"),sQuery(id+"F0.wireOp",EDGE,"E7.16.5"),sQuery(id+"F0.wireOp",EDGE,"E7.16.6"),sQuery(id+"F0.wireOp",EDGE,"E7.16.9"),sQuery(id+"F0.wireOp",EDGE,"E7.16.10"),sQuery(id+"F0.wireOp",EDGE,"E7.16.11"),sQuery(id+"F0.wireOp",EDGE,"E7.16.12"),sQuery(id+"F0.wireOp",EDGE,"E7.17.0"),sQuery(id+"F0.wireOp",EDGE,"E7.17.4"),sQuery(id+"F0.wireOp",EDGE,"E7.17.5"),sQuery(id+"F0.wireOp",EDGE,"E7.17.6"),sQuery(id+"F0.wireOp",EDGE,"E7.17.9"),sQuery(id+"F0.wireOp",EDGE,"E7.17.10"),sQuery(id+"F0.wireOp",EDGE,"E7.17.11"),sQuery(id+"F0.wireOp",EDGE,"E7.17.12"),sQuery(id+"F0.wireOp",EDGE,"E7.18.0"),sQuery(id+"F0.wireOp",EDGE,"E7.18.4"),sQuery(id+"F0.wireOp",EDGE,"E7.18.5"),sQuery(id+"F0.wireOp",EDGE,"E7.18.6"),sQuery(id+"F0.wireOp",EDGE,"E7.18.9"),sQuery(id+"F0.wireOp",EDGE,"E7.18.10"),sQuery(id+"F0.wireOp",EDGE,"E7.18.11"),sQuery(id+"F0.wireOp",EDGE,"E7.18.12"),sQuery(id+"F0.wireOp",EDGE,"E7.19.0"),sQuery(id+"F0.wireOp",EDGE,"E7.19.4"),sQuery(id+"F0.wireOp",EDGE,"E7.19.5"),sQuery(id+"F0.wireOp",EDGE,"E7.19.6"),sQuery(id+"F0.wireOp",EDGE,"E7.19.9"),sQuery(id+"F0.wireOp",EDGE,"E7.19.10"),sQuery(id+"F0.wireOp",EDGE,"E7.19.11"),sQuery(id+"F0.wireOp",EDGE,"E7.19.12")])],"isStart":false});
            var Q1;
            Q1=makeQuery(id+"F1.opExtrude","CAP_FACE",FACE,{"disambiguationData":[OSD([sQuery(id+"F0.wireOp",EDGE,"E0"),sQuery(id+"F0.wireOp",EDGE,"E2.bottom"),sQuery(id+"F0.wireOp",EDGE,"E2.top"),sQuery(id+"F0.wireOp",EDGE,"E2.left"),sQuery(id+"F0.wireOp",EDGE,"E2.right"),sQuery(id+"F0.wireOp",EDGE,"E3.filletArc"),sQuery(id+"F0.wireOp",EDGE,"E4.filletArc"),sQuery(id+"F0.wireOp",EDGE,"E5.filletArc"),sQuery(id+"F0.wireOp",EDGE,"E6.filletArc"),sQuery(id+"F0.wireOp",EDGE,"E7.1.0"),sQuery(id+"F0.wireOp",EDGE,"E7.1.4"),sQuery(id+"F0.wireOp",EDGE,"E7.1.5"),sQuery(id+"F0.wireOp",EDGE,"E7.1.6"),sQuery(id+"F0.wireOp",EDGE,"E7.1.9"),sQuery(id+"F0.wireOp",EDGE,"E7.1.10"),sQuery(id+"F0.wireOp",EDGE,"E7.1.11"),sQuery(id+"F0.wireOp",EDGE,"E7.1.12"),sQuery(id+"F0.wireOp",EDGE,"E7.2.0"),sQuery(id+"F0.wireOp",EDGE,"E7.2.4"),sQuery(id+"F0.wireOp",EDGE,"E7.2.5"),sQuery(id+"F0.wireOp",EDGE,"E7.2.6"),sQuery(id+"F0.wireOp",EDGE,"E7.2.9"),sQuery(id+"F0.wireOp",EDGE,"E7.2.10"),sQuery(id+"F0.wireOp",EDGE,"E7.2.11"),sQuery(id+"F0.wireOp",EDGE,"E7.2.12"),sQuery(id+"F0.wireOp",EDGE,"E7.3.0"),sQuery(id+"F0.wireOp",EDGE,"E7.3.4"),sQuery(id+"F0.wireOp",EDGE,"E7.3.5"),sQuery(id+"F0.wireOp",EDGE,"E7.3.6"),sQuery(id+"F0.wireOp",EDGE,"E7.3.9"),sQuery(id+"F0.wireOp",EDGE,"E7.3.10"),sQuery(id+"F0.wireOp",EDGE,"E7.3.11"),sQuery(id+"F0.wireOp",EDGE,"E7.3.12"),sQuery(id+"F0.wireOp",EDGE,"E7.4.0"),sQuery(id+"F0.wireOp",EDGE,"E7.4.4"),sQuery(id+"F0.wireOp",EDGE,"E7.4.5"),sQuery(id+"F0.wireOp",EDGE,"E7.4.6"),sQuery(id+"F0.wireOp",EDGE,"E7.4.9"),sQuery(id+"F0.wireOp",EDGE,"E7.4.10"),sQuery(id+"F0.wireOp",EDGE,"E7.4.11"),sQuery(id+"F0.wireOp",EDGE,"E7.4.12"),sQuery(id+"F0.wireOp",EDGE,"E7.5.0"),sQuery(id+"F0.wireOp",EDGE,"E7.5.4"),sQuery(id+"F0.wireOp",EDGE,"E7.5.5"),sQuery(id+"F0.wireOp",EDGE,"E7.5.6"),sQuery(id+"F0.wireOp",EDGE,"E7.5.9"),sQuery(id+"F0.wireOp",EDGE,"E7.5.10"),sQuery(id+"F0.wireOp",EDGE,"E7.5.11"),sQuery(id+"F0.wireOp",EDGE,"E7.5.12"),sQuery(id+"F0.wireOp",EDGE,"E7.6.0"),sQuery(id+"F0.wireOp",EDGE,"E7.6.4"),sQuery(id+"F0.wireOp",EDGE,"E7.6.5"),sQuery(id+"F0.wireOp",EDGE,"E7.6.6"),sQuery(id+"F0.wireOp",EDGE,"E7.6.9"),sQuery(id+"F0.wireOp",EDGE,"E7.6.10"),sQuery(id+"F0.wireOp",EDGE,"E7.6.11"),sQuery(id+"F0.wireOp",EDGE,"E7.6.12"),sQuery(id+"F0.wireOp",EDGE,"E7.7.0"),sQuery(id+"F0.wireOp",EDGE,"E7.7.4"),sQuery(id+"F0.wireOp",EDGE,"E7.7.5"),sQuery(id+"F0.wireOp",EDGE,"E7.7.6"),sQuery(id+"F0.wireOp",EDGE,"E7.7.9"),sQuery(id+"F0.wireOp",EDGE,"E7.7.10"),sQuery(id+"F0.wireOp",EDGE,"E7.7.11"),sQuery(id+"F0.wireOp",EDGE,"E7.7.12"),sQuery(id+"F0.wireOp",EDGE,"E7.8.0"),sQuery(id+"F0.wireOp",EDGE,"E7.8.4"),sQuery(id+"F0.wireOp",EDGE,"E7.8.5"),sQuery(id+"F0.wireOp",EDGE,"E7.8.6"),sQuery(id+"F0.wireOp",EDGE,"E7.8.9"),sQuery(id+"F0.wireOp",EDGE,"E7.8.10"),sQuery(id+"F0.wireOp",EDGE,"E7.8.11"),sQuery(id+"F0.wireOp",EDGE,"E7.8.12"),sQuery(id+"F0.wireOp",EDGE,"E7.9.0"),sQuery(id+"F0.wireOp",EDGE,"E7.9.4"),sQuery(id+"F0.wireOp",EDGE,"E7.9.5"),sQuery(id+"F0.wireOp",EDGE,"E7.9.6"),sQuery(id+"F0.wireOp",EDGE,"E7.9.9"),sQuery(id+"F0.wireOp",EDGE,"E7.9.10"),sQuery(id+"F0.wireOp",EDGE,"E7.9.11"),sQuery(id+"F0.wireOp",EDGE,"E7.9.12"),sQuery(id+"F0.wireOp",EDGE,"E7.10.0"),sQuery(id+"F0.wireOp",EDGE,"E7.10.4"),sQuery(id+"F0.wireOp",EDGE,"E7.10.5"),sQuery(id+"F0.wireOp",EDGE,"E7.10.6"),sQuery(id+"F0.wireOp",EDGE,"E7.10.9"),sQuery(id+"F0.wireOp",EDGE,"E7.10.10"),sQuery(id+"F0.wireOp",EDGE,"E7.10.11"),sQuery(id+"F0.wireOp",EDGE,"E7.10.12"),sQuery(id+"F0.wireOp",EDGE,"E7.11.0"),sQuery(id+"F0.wireOp",EDGE,"E7.11.4"),sQuery(id+"F0.wireOp",EDGE,"E7.11.5"),sQuery(id+"F0.wireOp",EDGE,"E7.11.6"),sQuery(id+"F0.wireOp",EDGE,"E7.11.9"),sQuery(id+"F0.wireOp",EDGE,"E7.11.10"),sQuery(id+"F0.wireOp",EDGE,"E7.11.11"),sQuery(id+"F0.wireOp",EDGE,"E7.11.12"),sQuery(id+"F0.wireOp",EDGE,"E7.12.0"),sQuery(id+"F0.wireOp",EDGE,"E7.12.4"),sQuery(id+"F0.wireOp",EDGE,"E7.12.5"),sQuery(id+"F0.wireOp",EDGE,"E7.12.6"),sQuery(id+"F0.wireOp",EDGE,"E7.12.9"),sQuery(id+"F0.wireOp",EDGE,"E7.12.10"),sQuery(id+"F0.wireOp",EDGE,"E7.12.11"),sQuery(id+"F0.wireOp",EDGE,"E7.12.12"),sQuery(id+"F0.wireOp",EDGE,"E7.13.0"),sQuery(id+"F0.wireOp",EDGE,"E7.13.4"),sQuery(id+"F0.wireOp",EDGE,"E7.13.5"),sQuery(id+"F0.wireOp",EDGE,"E7.13.6"),sQuery(id+"F0.wireOp",EDGE,"E7.13.9"),sQuery(id+"F0.wireOp",EDGE,"E7.13.10"),sQuery(id+"F0.wireOp",EDGE,"E7.13.11"),sQuery(id+"F0.wireOp",EDGE,"E7.13.12"),sQuery(id+"F0.wireOp",EDGE,"E7.14.0"),sQuery(id+"F0.wireOp",EDGE,"E7.14.4"),sQuery(id+"F0.wireOp",EDGE,"E7.14.5"),sQuery(id+"F0.wireOp",EDGE,"E7.14.6"),sQuery(id+"F0.wireOp",EDGE,"E7.14.9"),sQuery(id+"F0.wireOp",EDGE,"E7.14.10"),sQuery(id+"F0.wireOp",EDGE,"E7.14.11"),sQuery(id+"F0.wireOp",EDGE,"E7.14.12"),sQuery(id+"F0.wireOp",EDGE,"E7.15.0"),sQuery(id+"F0.wireOp",EDGE,"E7.15.4"),sQuery(id+"F0.wireOp",EDGE,"E7.15.5"),sQuery(id+"F0.wireOp",EDGE,"E7.15.6"),sQuery(id+"F0.wireOp",EDGE,"E7.15.9"),sQuery(id+"F0.wireOp",EDGE,"E7.15.10"),sQuery(id+"F0.wireOp",EDGE,"E7.15.11"),sQuery(id+"F0.wireOp",EDGE,"E7.15.12"),sQuery(id+"F0.wireOp",EDGE,"E7.16.0"),sQuery(id+"F0.wireOp",EDGE,"E7.16.4"),sQuery(id+"F0.wireOp",EDGE,"E7.16.5"),sQuery(id+"F0.wireOp",EDGE,"E7.16.6"),sQuery(id+"F0.wireOp",EDGE,"E7.16.9"),sQuery(id+"F0.wireOp",EDGE,"E7.16.10"),sQuery(id+"F0.wireOp",EDGE,"E7.16.11"),sQuery(id+"F0.wireOp",EDGE,"E7.16.12"),sQuery(id+"F0.wireOp",EDGE,"E7.17.0"),sQuery(id+"F0.wireOp",EDGE,"E7.17.4"),sQuery(id+"F0.wireOp",EDGE,"E7.17.5"),sQuery(id+"F0.wireOp",EDGE,"E7.17.6"),sQuery(id+"F0.wireOp",EDGE,"E7.17.9"),sQuery(id+"F0.wireOp",EDGE,"E7.17.10"),sQuery(id+"F0.wireOp",EDGE,"E7.17.11"),sQuery(id+"F0.wireOp",EDGE,"E7.17.12"),sQuery(id+"F0.wireOp",EDGE,"E7.18.0"),sQuery(id+"F0.wireOp",EDGE,"E7.18.4"),sQuery(id+"F0.wireOp",EDGE,"E7.18.5"),sQuery(id+"F0.wireOp",EDGE,"E7.18.6"),sQuery(id+"F0.wireOp",EDGE,"E7.18.9"),sQuery(id+"F0.wireOp",EDGE,"E7.18.10"),sQuery(id+"F0.wireOp",EDGE,"E7.18.11"),sQuery(id+"F0.wireOp",EDGE,"E7.18.12"),sQuery(id+"F0.wireOp",EDGE,"E7.19.0"),sQuery(id+"F0.wireOp",EDGE,"E7.19.4"),sQuery(id+"F0.wireOp",EDGE,"E7.19.5"),sQuery(id+"F0.wireOp",EDGE,"E7.19.6"),sQuery(id+"F0.wireOp",EDGE,"E7.19.9"),sQuery(id+"F0.wireOp",EDGE,"E7.19.10"),sQuery(id+"F0.wireOp",EDGE,"E7.19.11"),sQuery(id+"F0.wireOp",EDGE,"E7.19.12")])],"isStart":true});
            fillet(context, id + "F2", {"entities" : qUnion([Q0, Q1]), "radius" : 0.2 * mm, "tangentPropagation" : true, "allowEdgeOverflow" : false});
        }
    });
